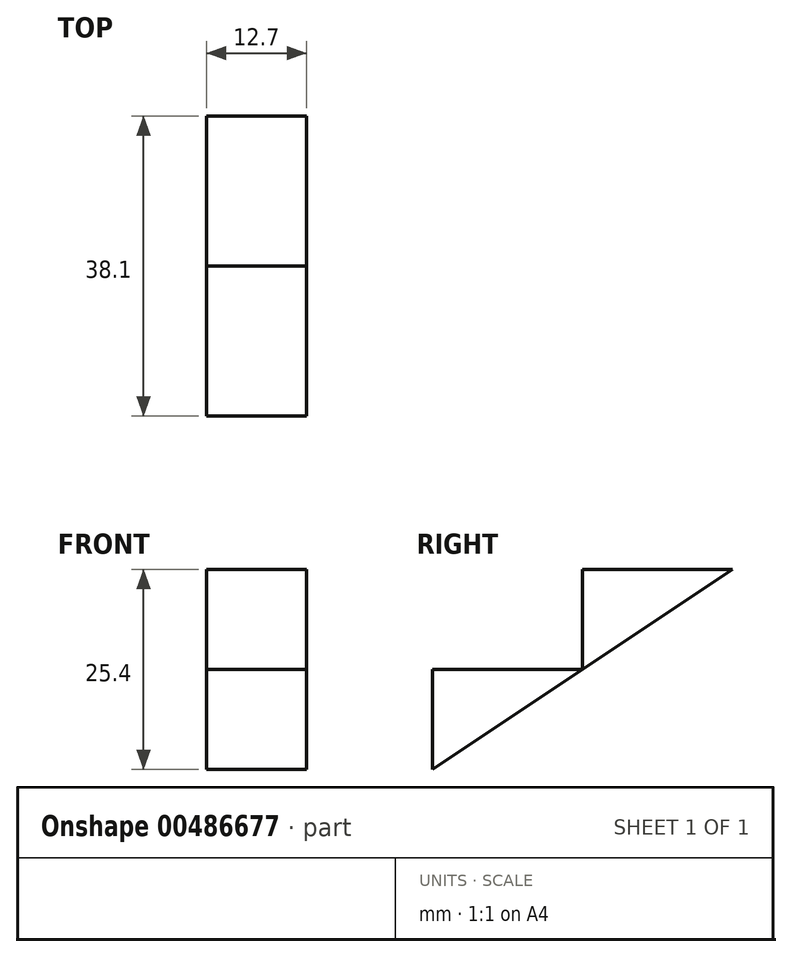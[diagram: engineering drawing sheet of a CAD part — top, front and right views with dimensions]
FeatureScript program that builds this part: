
annotation { "Feature Type Name" : "Feature", "Feature Type Description" : "" }
export const myFeature = defineFeature(function(context is Context, id is Id, definition is map)
    precondition{}
    {
        {
            var Q0;
            Q0=qCreatedBy(makeId("Right.planeOp"),FACE);
            var sketch = newSketch(context, id + "F0", { "sketchPlane" : qUnion([Q0])});
            skLineSegment(sketch, "E0", {"start": v(38.1, 14.23) * mm, "end": v(19.05, 14.23) * mm});
            skLineSegment(sketch, "E1", {"start": v(19.05, 14.23) * mm, "end": v(19.05, 1.53) * mm});
            skLineSegment(sketch, "E2", {"start": v(19.05, 1.53) * mm, "end": v(38.1, 14.23) * mm});
            skLineSegment(sketch, "E3", {"start": v(19.05, 1.53) * mm, "end": v(0, 1.53) * mm});
            skLineSegment(sketch, "E4", {"start": v(0, 1.53) * mm, "end": v(0, -11.17) * mm});
            skLineSegment(sketch, "E5", {"start": v(0, -11.17) * mm, "end": v(19.05, 1.53) * mm});
            skSolve(sketch);
        }
        {
            var Q0;
            Q0 = qSketchRegion(id + "F0", true);
            extrude(context, id + "F1", {"entities" : qUnion([Q0]), "depth" : 12.7 * mm});
        }
    });
